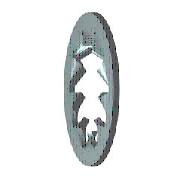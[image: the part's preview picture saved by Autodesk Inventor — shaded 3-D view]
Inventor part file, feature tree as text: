
AUTODESK INVENTOR PART (.ipt)
format: ipt  version: 2011 SP1 (Build 150282100, 282)  size: 160,256 bytes
history: native  units: mm (DEFAULTED — no unit token found)
features: extrude x1, pattern_circular x1, plane x1
ambient origin geometry x7: Origin, YZ Plane, XY Plane, X Axis, Y Axis, Z Axis, Center Point
bodies: Solid1 (feature_tree), Body (feature_tree)
feature tree (3):
  extrude  "Cut"  Depth=11.0mm
  pattern_circular  "Cuts"  [2 undecoded]
  plane  "Work Plane1"
note: 2 required parameter values undecoded (feature->parameter linkage not recoverable at this tier; creation-order binding heuristic only, values carry confidence <= 0.55)
